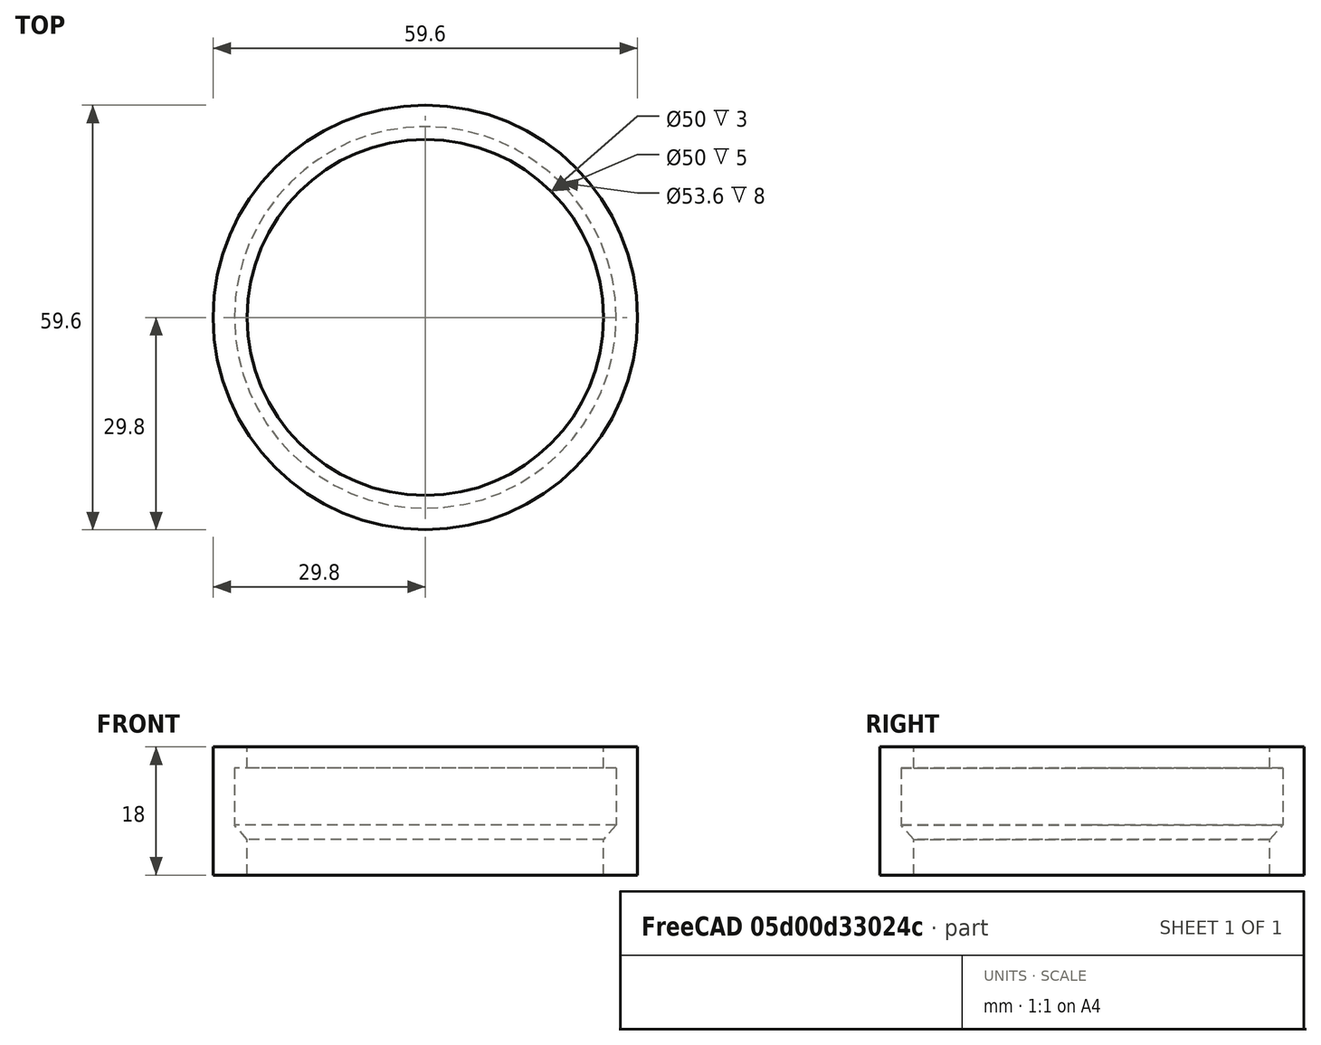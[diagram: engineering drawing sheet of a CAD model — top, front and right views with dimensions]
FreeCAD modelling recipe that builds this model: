
FCSTD DOCUMENT  (FreeCAD 1.1R39748 (Git))
Label: горло
License: All rights reserved
LicenseURL: https://en.wikipedia.org/wiki/All_rights_reserved
objects: App::Point×1, Sketcher::SketchObject×1, PartDesign::Revolution×1, PartDesign::Body×1
note: 6 computed .brp shape members not serialized (recipe doc carries the construction recipe); baked Part::Feature solids carry a one-line shape summary decoded from their .brp

FEATURE [App::Point] Origin001
  Role = Origin
FEATURE [Sketcher::SketchObject] Sketch
  ArcFitTolerance = 1e-06
  AttachmentSupport = -> [XZ_Plane]
  ExternalTypes = [0]
  FullyConstrained = true
  MakeInternals = false
  MapMode = 5
  Placement = pos=(0,0,0) rot=(1,0,0;1.5708rad)
  expr: Constraints[23] = 63 / 2 - 1.8
  expr: Constraints[25] = 29.7 * 2
  expr: Constraints[2] = 50 / 2
  sketch-geometry (8):
    g0: LineSegment StartX=25 StartY=0 StartZ=0 EndX=25 EndY=5 EndZ=0
    g1: LineSegment StartX=29.7 StartY=17.7 StartZ=0 EndX=29.7 EndY=9.7 EndZ=0
    g2: LineSegment StartX=29.7 StartY=9.7 StartZ=0 EndX=25 EndY=5 EndZ=0
    g3: LineSegment StartX=29.7 StartY=17.7 StartZ=0 EndX=25 EndY=17.7 EndZ=0
    g4: LineSegment StartX=25 StartY=17.7 StartZ=0 EndX=25 EndY=20.7 EndZ=0
    g5: LineSegment StartX=25 StartY=20.7 StartZ=0 EndX=32.7 EndY=20.7 EndZ=0
    g6: LineSegment StartX=32.7 StartY=20.7 StartZ=0 EndX=32.7 EndY=0 EndZ=0
    g7: LineSegment StartX=32.7 StartY=0 StartZ=0 EndX=25 EndY=0 EndZ=0
  constraints (26):
    c: PointOnObject(g0,g-1)
    c: Vertical(g0)
    c: Distance(g0,g-1) = 25
    c: Vertical(g1)
    c: Coincident(g2,g0)
    c: Coincident(g1,g2)
    c: Distance(g1,g1) = 8
    c: Coincident(g3,g1)
    c: Horizontal(g3)
    c: DistanceX(g-1,g3) = 25
    c: Coincident(g4,g3)
    c: Vertical(g4)
    c: Coincident(g5,g4)
    c: Horizontal(g5)
    c: Coincident(g6,g5)
    c: PointOnObject(g6,g-1)
    c: Vertical(g6)
    c: Coincident(g7,g6)
    c: Coincident(g7,g0)
    c: Distance(g3,g4) = 3
    c: DistanceX(g1,g6) = 3
    c: DistanceY(g0,g0) = 5
    c: Angle(g0,g2) = 2.35619
    c: DistanceX(g-1,g1) = 29.7
    c: Distance(g3,g1) = 4.7
    c: DistanceX(g-1,g1) = 59.4
FEATURE [PartDesign::Revolution] Revolution
  Angle = 360
  Angle2 = 60
  Axis = (0,2e-16,1)
  Base = (0,0,0)
  Placement = pos=(0,0,0) rot=(1,0,0;1.5708rad)
  Profile = -> Sketch
  ReferenceAxis = -> Sketch [V_Axis]
  Reversed = true
  Suppressed = false
  Type = 0
FEATURE [PartDesign::Body] Body
  AllowCompound = false
  Group = -> [Sketch,Revolution]
  Origin = -> Origin
  Tip = -> Revolution
